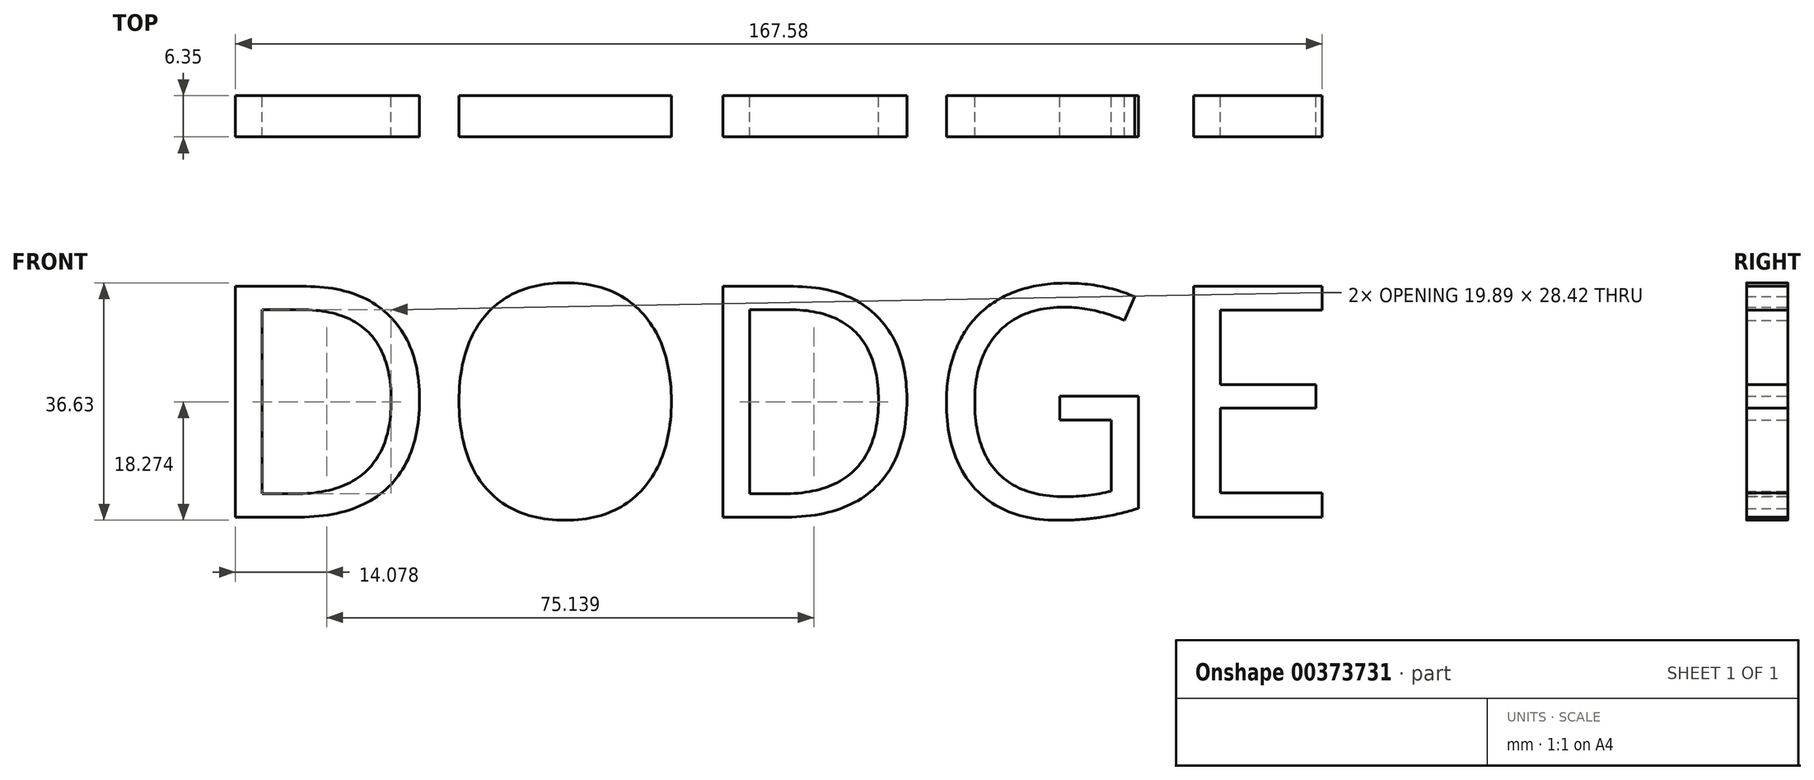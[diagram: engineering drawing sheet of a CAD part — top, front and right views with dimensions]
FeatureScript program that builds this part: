
annotation { "Feature Type Name" : "Feature", "Feature Type Description" : "" }
export const myFeature = defineFeature(function(context is Context, id is Id, definition is map)
    precondition{}
    {
        {
            var Q0;
            Q0=qCreatedBy(makeId("Front.planeOp"),FACE);
            var sketch = newSketch(context, id + "F0", { "sketchPlane" : qUnion([Q0])});
            skText(sketch, "E0", { "text": "DODGE\n", "fontName": "OpenSans-Regular.ttf"});
            const initialGuessF0  = {"E0": [-0.03588, -0.01723, 1, 0, 0.03588]};
            skSetInitialGuess(sketch, initialGuessF0);
            skSolve(sketch);
        }
        {
            var Q0;
            Q0=makeQuery(id+"F0.imprint","IMPRINT",FACE,{"disambiguationData":[TD([[makeQuery(id+"F0.imprint","IMPRINT",EDGE,{"derivedFrom":sQuery(id+"F0.wireOp",EDGE,"E0.sketch_text.stroke-22")}),1.0]])]});
            var Q1;
            Q1 = qSketchRegion(id + "F0", true);
            extrude(context, id + "F1", {"entities" : qUnion([Q0, Q1]), "depth" : 6.35 * mm});
        }
    });
